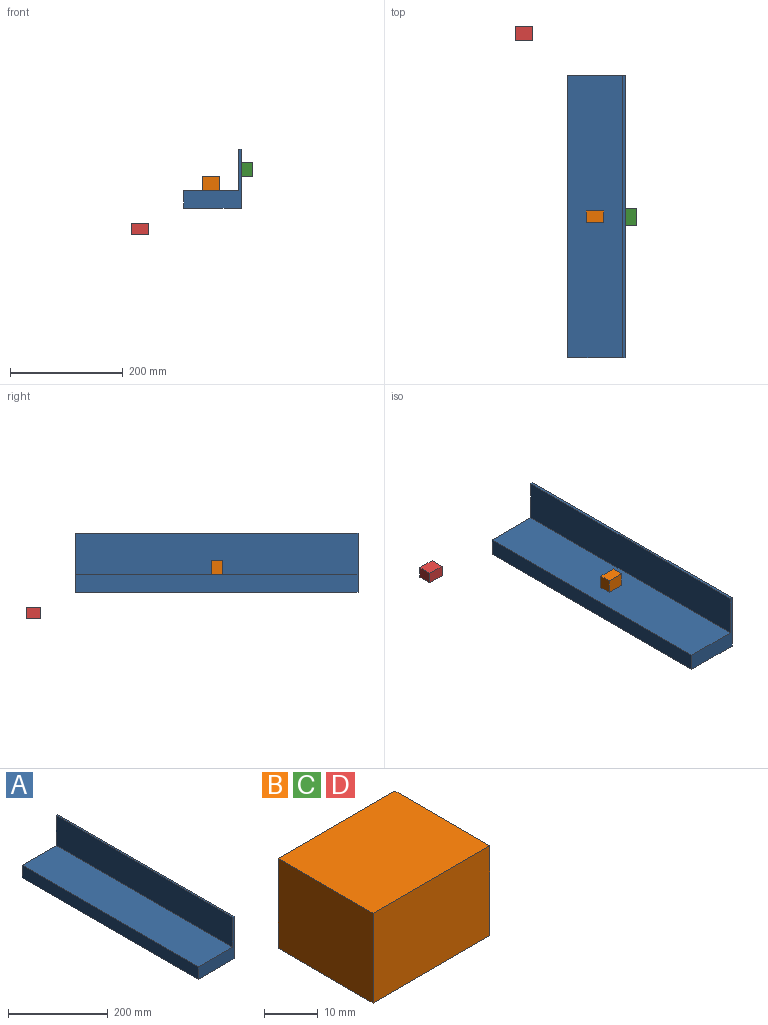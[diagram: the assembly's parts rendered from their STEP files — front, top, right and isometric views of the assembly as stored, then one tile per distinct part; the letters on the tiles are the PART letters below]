
ASSEMBLY  parts=4 mates=2
PART A: 8 faces, bbox 101.6x500x104.5 mm
  f0: plane 500x104.55mm, normal (1,0,0), area 52272.6mm2, adj f1,f5,f6,f7
  f1: plane 500x4.64mm, normal (0,0,1), area 2319.5mm2, adj f0,f2,f6,f7
  f2: plane 500x73.73mm, normal (-1,0,0), area 36864.5mm2, adj f1,f3,f6,f7
  f3: plane 500x97mm, normal (0,0,1), area 48499.1mm2, adj f2,f4,f6,f7
  f4: plane 500x30.82mm, normal (-1,0,0), area 15408.1mm2, adj f3,f5,f6,f7
  f5: plane 500x101.64mm, normal (0,0,-1), area 50818.6mm2, adj f0,f4,f6,f7
  f6: plane 104.55x101.64mm, normal (0,-1,0), area 3474.1mm2, adj f0,f1,f2,f3,f4,f5
  f7: plane 104.55x101.64mm, normal (0,1,0), area 3474.1mm2, adj f0,f1,f2,f3,f4,f5
PART B: 6 faces, bbox 30.8x25x20.5 mm
  f0: plane 25x20.49mm, normal (-1,0,0), area 512.1mm2, adj f1,f3,f4,f5
  f1: plane 30.79x25mm, normal (0,0,-1), area 769.7mm2, adj f0,f2,f4,f5
  f2: plane 25x20.49mm, normal (1,0,0), area 512.1mm2, adj f1,f3,f4,f5
  f3: plane 30.79x25mm, normal (0,0,1), area 769.7mm2, adj f0,f2,f4,f5
  f4: plane 30.79x20.49mm, normal (0,-1,0), area 630.7mm2, adj f0,f1,f2,f3
  f5: plane 30.79x20.49mm, normal (0,1,0), area 630.7mm2, adj f0,f1,f2,f3
PART C: same geometry as B
PART D: same geometry as B
PLACE A at identity fixed
PLACE B rot(axis=(1,0,0),90deg) t=(33.11,-239.76,55.82)mm
PLACE C rot(axis=(0.58,-0.58,-0.58),120deg) t=(122.12,-234.61,80.43)mm
PLACE D t=(-92.83,88.03,-47.37)mm
MATE fastened B.f4 <-> A.f3  axis (0,0,-1) through (48.5,-250,30.82)mm
MATE slider A.f1 <-> C.f5  axis (0,0,1) through (101.64,-250,104.55)mm
